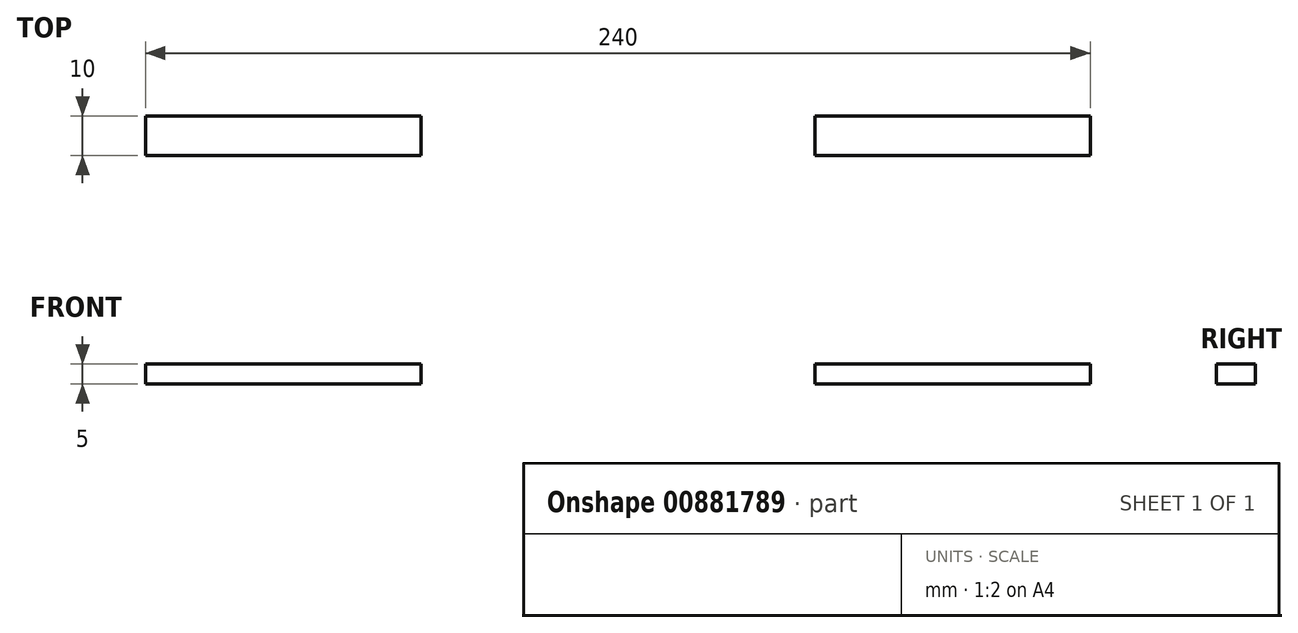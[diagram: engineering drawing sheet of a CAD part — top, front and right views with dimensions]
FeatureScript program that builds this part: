
annotation { "Feature Type Name" : "Feature", "Feature Type Description" : "" }
export const myFeature = defineFeature(function(context is Context, id is Id, definition is map)
    precondition{}
    {
        {
            var Q0;
            Q0=qCreatedBy(makeId("Top.planeOp"),FACE);
            var sketch = newSketch(context, id + "F0", { "sketchPlane" : qUnion([Q0])});
            skLineSegment(sketch, "E0.bottom", {"start": v(120, -32.5) * mm, "end": v(-120, -32.5) * mm});
            skLineSegment(sketch, "E0.top", {"start": v(120, 32.5) * mm, "end": v(-120, 32.5) * mm});
            skLineSegment(sketch, "E0.left", {"start": v(120, -32.5) * mm, "end": v(120, 32.5) * mm});
            skLineSegment(sketch, "E0.right", {"start": v(-120, -32.5) * mm, "end": v(-120, 32.5) * mm});
            skPoint(sketch, "E0.middle", {"position": v(0, 0) * mm});
            skLineSegment(sketch, "E1", {"start": v(0, 32.5) * mm, "end": v(0, 27.14) * mm, "construction": true});
            skLineSegment(sketch, "E2", {"start": v(-120, 0) * mm, "end": v(-109.37, 0) * mm, "construction": true});
            skLineSegment(sketch, "E3", {"start": v(-50, 32.5) * mm, "end": v(-50, 22.5) * mm});
            skLineSegment(sketch, "E4", {"start": v(-50, 22.5) * mm, "end": v(-120, 22.5) * mm});
            skLineSegment(sketch, "E5", {"start": v(-50, 32.5) * mm, "end": v(-120, 32.5) * mm});
            skLineSegment(sketch, "E6.MirrorCS", {"start": v(50, 32.5) * mm, "end": v(50, 22.5) * mm});
            skLineSegment(sketch, "E7.MirrorCS", {"start": v(50, 22.5) * mm, "end": v(120, 22.5) * mm});
            skLineSegment(sketch, "E8", {"start": v(-120, 22.5) * mm, "end": v(-120, 32.5) * mm});
            skLineSegment(sketch, "E9.MirrorCS", {"start": v(120, 22.5) * mm, "end": v(120, 32.5) * mm});
            skLineSegment(sketch, "E10.MirrorCS", {"start": v(50, 32.5) * mm, "end": v(120, 32.5) * mm});
            skLineSegment(sketch, "E11.MirrorCS", {"start": v(-50, -22.5) * mm, "end": v(-120, -22.5) * mm});
            skLineSegment(sketch, "E12.MirrorCS", {"start": v(-50, -32.5) * mm, "end": v(-50, -22.5) * mm});
            skLineSegment(sketch, "E13.MirrorCS", {"start": v(-50, -32.5) * mm, "end": v(-120, -32.5) * mm});
            skLineSegment(sketch, "E14.MirrorCS", {"start": v(-120, -22.5) * mm, "end": v(-120, -32.5) * mm});
            skLineSegment(sketch, "E15.MirrorCS", {"start": v(50, -22.5) * mm, "end": v(120, -22.5) * mm});
            skLineSegment(sketch, "E16.MirrorCS", {"start": v(50, -32.5) * mm, "end": v(50, -22.5) * mm});
            skLineSegment(sketch, "E17.MirrorCS", {"start": v(50, -32.5) * mm, "end": v(120, -32.5) * mm});
            skLineSegment(sketch, "E18.MirrorCS", {"start": v(120, 32.5) * mm, "end": v(120, -32.5) * mm});
            skSolve(sketch);
        }
        {
            var Q0;
            Q0=makeQuery(id+"F0.imprint","IMPRINT",FACE,{"disambiguationData":[TD([[makeQuery(id+"F0.imprint","IMPRINT",EDGE,{"derivedFrom":sQuery(id+"F0.wireOp",EDGE,"E0.bottom")}),-1.0]])]});
            extrude(context, id + "F1", {"entities" : qUnion([Q0]), "depth" : 5 * mm, "offsetDistance" : 25 * mm});
        }
    });
